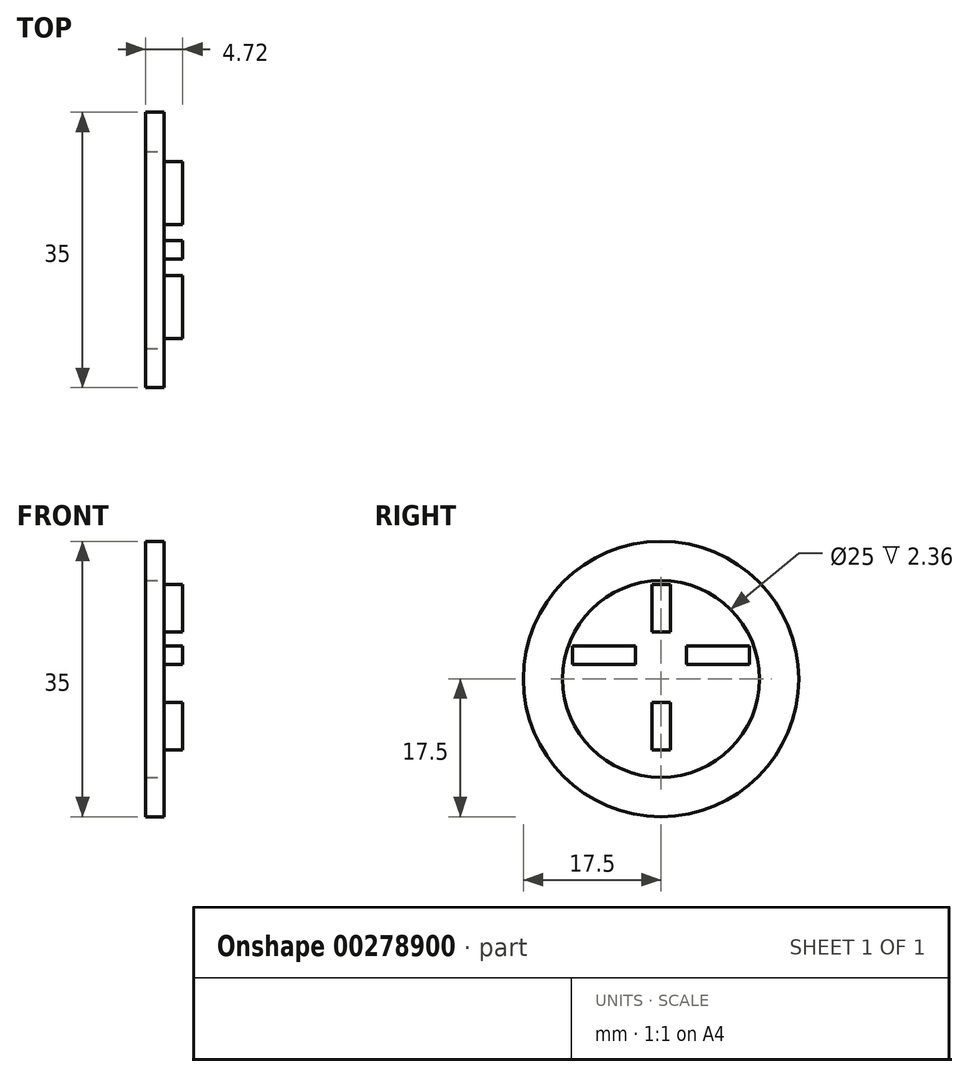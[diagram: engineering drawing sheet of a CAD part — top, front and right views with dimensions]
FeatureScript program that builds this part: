
annotation { "Feature Type Name" : "Feature", "Feature Type Description" : "" }
export const myFeature = defineFeature(function(context is Context, id is Id, definition is map)
    precondition{}
    {
        {
            assignVariable(context, id + "F0", {"name" : "t", "anyValue" : 2.36});
        }
        {
            var Q0;
            Q0=qCreatedBy(makeId("Top.planeOp"),FACE);
            var sketch = newSketch(context, id + "F1", { "sketchPlane" : qUnion([Q0])});
            skLineSegment(sketch, "E0", {"start": v(2.36, 11.25) * mm, "end": v(0, 11.25) * mm});
            skLineSegment(sketch, "E1", {"start": v(2.36, -11.25) * mm, "end": v(0, -11.25) * mm});
            skLineSegment(sketch, "E2", {"start": v(0, -10) * mm, "end": v(0, -11.25) * mm});
            skLineSegment(sketch, "E3", {"start": v(0, 11.25) * mm, "end": v(0, 0) * mm, "construction": true});
            skLineSegment(sketch, "E4", {"start": v(0, 0) * mm, "end": v(0, -11.25) * mm, "construction": true});
            skLineSegment(sketch, "E5", {"start": v(2.36, 3.25) * mm, "end": v(0, 3.25) * mm});
            skLineSegment(sketch, "E6", {"start": v(2.36, -3.25) * mm, "end": v(0, -3.25) * mm});
            skLineSegment(sketch, "E7", {"start": v(2.36, 11.25) * mm, "end": v(2.36, 3.25) * mm});
            skLineSegment(sketch, "E8", {"start": v(2.36, -3.25) * mm, "end": v(2.36, -11.25) * mm});
            skLineSegment(sketch, "E9", {"start": v(0, 11.25) * mm, "end": v(-3.75, 11.25) * mm});
            skLineSegment(sketch, "E10", {"start": v(0, -11.25) * mm, "end": v(-3.75, -11.25) * mm});
            skArc(sketch, "E11", {"start": v(-3.75, 11.25) * mm, "mid": v(-15, 0) * mm, "end": v(-3.75, -11.25) * mm});
            skLineSegment(sketch, "E12", {"start": v(0, 3.25) * mm, "end": v(0, -3.25) * mm});
            skSolve(sketch);
        }
        {
            var Q0;
            Q0 = qSketchRegion(id + "F1", true);
            extrude(context, id + "F2", {"entities" : qUnion([Q0]), "endBound" : BoundingType.SYMMETRIC, "depth" : (getVariable(context, 't')) * mm});
        }
        {
            var Q0;
            Q0=qCreatedBy(makeId("Front.planeOp"),FACE);
            var sketch = newSketch(context, id + "F3", { "sketchPlane" : qUnion([Q0])});
            skLineSegment(sketch, "E13", {"start": v(2.36, 9) * mm, "end": v(0, 9) * mm});
            skLineSegment(sketch, "E14", {"start": v(-3, 9) * mm, "end": v(-3, 12) * mm});
            skLineSegment(sketch, "E15", {"start": v(2.36, -12) * mm, "end": v(0, -12) * mm});
            skLineSegment(sketch, "E16", {"start": v(0, -12) * mm, "end": v(-3, -12) * mm});
            skLineSegment(sketch, "E17", {"start": v(-3, 9) * mm, "end": v(-3, -9) * mm, "construction": true});
            skArc(sketch, "E18", {"start": v(-3, 12) * mm, "mid": v(-15, 0) * mm, "end": v(-3, -12) * mm});
            skLineSegment(sketch, "E19", {"start": v(2.36, 3) * mm, "end": v(0, 3) * mm});
            skLineSegment(sketch, "E20", {"start": v(0, 3) * mm, "end": v(0, -6) * mm});
            skLineSegment(sketch, "E21", {"start": v(0, -6) * mm, "end": v(2.36, -6) * mm});
            skLineSegment(sketch, "E22", {"start": v(2.36, 3) * mm, "end": v(2.36, 9) * mm});
            skLineSegment(sketch, "E23", {"start": v(2.36, -6) * mm, "end": v(2.36, -12) * mm});
            skLineSegment(sketch, "E24", {"start": v(-3, 9) * mm, "end": v(0, 9) * mm});
            skSolve(sketch);
        }
        {
            var Q0;
            Q0 = qSketchRegion(id + "F3", true);
            extrude(context, id + "F4", {"entities" : qUnion([Q0]), "endBound" : BoundingType.SYMMETRIC, "depth" : (getVariable(context, 't')) * mm});
        }
        {
            var Q0;
            Q0=qCreatedBy(makeId("Top.planeOp"),FACE);
            var sketch = newSketch(context, id + "F5", { "sketchPlane" : qUnion([Q0])});
            skLineSegment(sketch, "E25", {"start": v(-6.64, 0) * mm, "end": v(-6.64, 1.18) * mm});
            skLineSegment(sketch, "E26", {"start": v(-6.64, 1.18) * mm, "end": v(-18.64, 1.18) * mm});
            skLineSegment(sketch, "E27", {"start": v(-18.64, 1.18) * mm, "end": v(-18.64, -1.18) * mm});
            skLineSegment(sketch, "E28", {"start": v(-18.64, -1.18) * mm, "end": v(-6.64, -1.18) * mm});
            skLineSegment(sketch, "E29", {"start": v(-6.64, -1.18) * mm, "end": v(-6.64, 0) * mm});
            skSolve(sketch);
        }
        {
            var Q0;
            Q0 = qSketchRegion(id + "F5", true);
            extrude(context, id + "F6", {"entities" : qUnion([Q0]), "operationType" : NewBodyOperationType.REMOVE, "endBound" : BoundingType.THROUGH_ALL, "oppositeDirection" : true, "depth" : 25 * mm});
        }
        {
            var Q0;
            Q0=qCreatedBy(makeId("Right.planeOp"),FACE);
            var sketch = newSketch(context, id + "F7", { "sketchPlane" : qUnion([Q0])});
            skCircle(sketch, "E30", {"center": v(0, 0) * mm, "radius": 17.5 * mm});
            skSolve(sketch);
        }
        {
            var Q0;
            Q0=makeQuery(id+"F7.imprint","IMPRINT",FACE,{"disambiguationData":[TD([[makeQuery(id+"F7.imprint","IMPRINT",EDGE,{"derivedFrom":sQuery(id+"F7.wireOp",EDGE,"E30")}),1.0]])]});
            extrude(context, id + "F8", {"entities" : qUnion([Q0]), "oppositeDirection" : true, "depth" : (getVariable(context, 't')) * mm});
        }
        {
            var Q0;
            Q0=qCreatedBy(makeId("Right.planeOp"),FACE);
            var sketch = newSketch(context, id + "F9", { "sketchPlane" : qUnion([Q0])});
            skCircle(sketch, "E31", {"center": v(0, 0) * mm, "radius": 12.5 * mm});
            skSolve(sketch);
        }
        {
            var Q0;
            Q0 = qSketchRegion(id + "F9", true);
            extrude(context, id + "F10", {"entities" : qUnion([Q0]), "operationType" : NewBodyOperationType.REMOVE, "endBound" : BoundingType.THROUGH_ALL, "oppositeDirection" : true, "depth" : 25 * mm});
        }
        {
            var Q0;
            Q0=makeQuery(id+"F8.opExtrude","SWEPT_BODY",BODY,{"disambiguationData":[OSD([sQuery(id+"F7.wireOp",EDGE,"E30")])]});
            var Q1;
            Q1=qCreatedBy(makeId("Top.planeOp"),FACE);
            transform(context, id + "F11", {"entities" : qUnion([Q0]), "transformType" : TransformType.TRANSLATION_DISTANCE, "transformDirection" : qUnion([Q1]), "distance" : 3 * mm, "oppositeDirection" : true, "makeCopy" : false});
        }
        {
            var Q0;
            Q0 = qSketchRegion(id + "F5", true);
            extrude(context, id + "F12", {"entities" : qUnion([Q0]), "operationType" : NewBodyOperationType.REMOVE, "endBound" : BoundingType.THROUGH_ALL, "depth" : 25 * mm});
        }
        {
            var Q0;
            Q0=makeQuery(id+"F2.opExtrude","SWEPT_BODY",BODY,{"disambiguationData":[OSD([sQuery(id+"F1.wireOp",EDGE,"E0"),sQuery(id+"F1.wireOp",EDGE,"E1"),sQuery(id+"F1.wireOp",EDGE,"E3"),sQuery(id+"F1.wireOp",EDGE,"E4"),sQuery(id+"F1.wireOp",EDGE,"E5"),sQuery(id+"F1.wireOp",EDGE,"E6"),sQuery(id+"F1.wireOp",EDGE,"E7"),sQuery(id+"F1.wireOp",EDGE,"E8"),sQuery(id+"F1.wireOp",EDGE,"E9"),sQuery(id+"F1.wireOp",EDGE,"E10"),sQuery(id+"F1.wireOp",EDGE,"E11")])]});
            var Q1;
            Q1=makeQuery(id+"F4.opExtrude","SWEPT_BODY",BODY,{"disambiguationData":[OSD([sQuery(id+"F3.wireOp",EDGE,"E13"),sQuery(id+"F3.wireOp",EDGE,"tkBttHT2-JKYS-W1qo-QfgE-5mvWB0bdgSVI"),sQuery(id+"F3.wireOp",EDGE,"GjEdvTPp-NN5Z-msqy-WKqG-ZJEEbg38qRa4"),sQuery(id+"F3.wireOp",EDGE,"E14"),sQuery(id+"F3.wireOp",EDGE,"E15"),sQuery(id+"F3.wireOp",EDGE,"E16"),sQuery(id+"F3.wireOp",EDGE,"E18"),sQuery(id+"F3.wireOp",EDGE,"oocRwMNW-dP3u-5gmQ-rp1Y-YatCnYySc12P"),sQuery(id+"F3.wireOp",EDGE,"E19"),sQuery(id+"F3.wireOp",EDGE,"E20"),sQuery(id+"F3.wireOp",EDGE,"E21"),sQuery(id+"F3.wireOp",EDGE,"E22"),sQuery(id+"F3.wireOp",EDGE,"E23")])]});
            booleanBodies(context, id + "F13", {"operationType" : BooleanOperationType.SUBTRACTION, "tools" : qUnion([Q0]), "targets" : qUnion([Q1]), "keepTools" : true});
        }
    });
